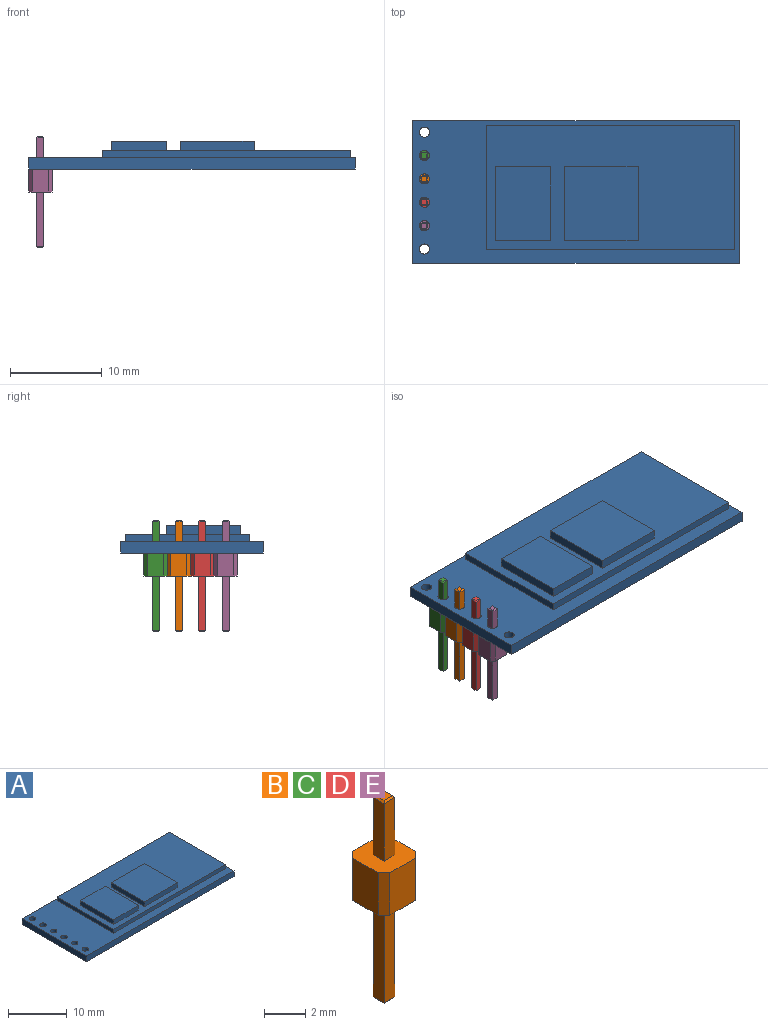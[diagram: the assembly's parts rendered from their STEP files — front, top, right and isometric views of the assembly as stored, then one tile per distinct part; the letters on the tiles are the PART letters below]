
ASSEMBLY  parts=5 mates=1
PART A: 27 faces, bbox 35.5x15.5x3 mm
  f0: plane 27x13.5mm, normal (0,0,1), area 252.5mm2, adj f13,f14,f15,f16,f17,f18,f19,f20
  f1: plane 35.5x1.2mm, normal (0,1,0), area 42.6mm2, adj f2,f10,f11,f12
  f2: plane 15.54x1.2mm, normal (-1,0,0), area 18.6mm2, adj f1,f3,f11,f12
  f3: plane 35.5x1.2mm, normal (0,-1,0), area 42.6mm2, adj f2,f10,f11,f12
  f4: cylinder r=0.55mm len=1.2mm, axis (0,0,-1), area 4.1mm2, adj f11,f12
  f5: cylinder r=0.55mm len=1.2mm, axis (0,0,-1), area 4.1mm2, adj f11,f12
  f6: cylinder r=0.55mm len=1.2mm, axis (0,0,-1), area 4.1mm2, adj f11,f12
  f7: cylinder r=0.55mm len=1.2mm, axis (0,0,-1), area 4.1mm2, adj f11,f12
  f8: cylinder r=0.55mm len=1.2mm, axis (0,0,-1), area 4.1mm2, adj f11,f12
  f9: cylinder r=0.55mm len=1.2mm, axis (0,0,-1), area 4.1mm2, adj f11,f12
  f10: plane 15.54x1.2mm, normal (1,0,0), area 18.6mm2, adj f1,f3,f11,f12
  f11: plane 35.5x15.54mm, normal (0,0,1), area 181.5mm2, adj f1,f2,f3,f4,f5,f6,f7,f8
  f12: plane 35.5x15.54mm, normal (0,0,-1), area 546mm2, adj f1,f2,f3,f4,f5,f6,f7,f8
  f13: plane 13.5x0.8mm, normal (-1,0,0), area 10.8mm2, adj f0,f11,f14,f16
  f14: plane 27x0.8mm, normal (0,-1,0), area 21.6mm2, adj f0,f11,f13,f15
  f15: plane 13.5x0.8mm, normal (1,0,0), area 10.8mm2, adj f0,f11,f14,f16
  f16: plane 27x0.8mm, normal (0,1,0), area 21.6mm2, adj f0,f11,f13,f15
  f17: plane 8x1mm, normal (-1,0,0), area 8mm2, adj f0,f18,f20,f21
  f18: plane 6x1mm, normal (0,-1,0), area 6mm2, adj f0,f17,f19,f21
  f19: plane 8x1mm, normal (1,0,0), area 8mm2, adj f0,f18,f20,f21
  f20: plane 6x1mm, normal (0,1,0), area 6mm2, adj f0,f17,f19,f21
  f21: plane 8x6mm, normal (0,0,1), area 48mm2, adj f17,f18,f19,f20
  f22: plane 8x1mm, normal (-1,0,0), area 8mm2, adj f0,f23,f25,f26
  f23: plane 8x1mm, normal (0,-1,0), area 8mm2, adj f0,f22,f24,f26
  f24: plane 8x1mm, normal (1,0,0), area 8mm2, adj f0,f23,f25,f26
  f25: plane 8x1mm, normal (0,1,0), area 8mm2, adj f0,f22,f24,f26
  f26: plane 8x8mm, normal (0,0,1), area 64mm2, adj f22,f23,f24,f25
PART B: 28 faces, bbox 2.5x2.5x12 mm
  f0: plane 3.4x0.75mm, normal (0,-1,0), area 2.6mm2, adj f1,f3,f5,f13
  f1: plane 3.4x0.75mm, normal (1,0,0), area 2.6mm2, adj f0,f2,f6,f13
  f2: plane 3.4x0.75mm, normal (0,1,0), area 2.6mm2, adj f1,f3,f8,f13
  f3: plane 3.4x0.75mm, normal (-1,0,0), area 2.6mm2, adj f0,f2,f7,f13
  f4: plane 0.55x0.55mm, normal (0,0,1), area 0.3mm2, adj f5,f6,f7,f8
  f5: plane 0.75x0.1mm, normal (0,-0.71,0.71), area 0.1mm2, adj f0,f4,f6,f7
  f6: plane 0.75x0.1mm, normal (0.71,0,0.71), area 0.1mm2, adj f1,f4,f5,f8
  f7: plane 0.75x0.1mm, normal (-0.71,0,0.71), area 0.1mm2, adj f3,f4,f5,f8
  f8: plane 0.75x0.1mm, normal (0,0.71,0.71), area 0.1mm2, adj f2,f4,f6,f7
  f9: plane 2.5x1.74mm, normal (0,-1,0), area 4.4mm2, adj f13,f14,f25,f27
  f10: plane 2.5x1.74mm, normal (1,0,0), area 4.4mm2, adj f13,f14,f24,f25
  f11: plane 2.5x1.74mm, normal (0,1,0), area 4.4mm2, adj f13,f14,f24,f26
  f12: plane 2.5x1.74mm, normal (-1,0,0), area 4.4mm2, adj f13,f14,f26,f27
  f13: plane 2.54x2.54mm, normal (0,0,1), area 5.6mm2, adj f0,f1,f2,f3,f9,f10,f11,f12
  f14: plane 2.54x2.54mm, normal (0,0,-1), area 5.6mm2, adj f9,f10,f11,f12,f20,f21,f22,f23
  f15: plane 0.55x0.55mm, normal (0,0,-1), area 0.3mm2, adj f16,f17,f18,f19
  f16: plane 0.75x0.1mm, normal (0,-0.71,-0.71), area 0.1mm2, adj f15,f17,f19,f23
  f17: plane 0.75x0.1mm, normal (0.71,0,-0.71), area 0.1mm2, adj f15,f16,f18,f22
  f18: plane 0.75x0.1mm, normal (0,0.71,-0.71), area 0.1mm2, adj f15,f17,f19,f21
  f19: plane 0.75x0.1mm, normal (-0.71,0,-0.71), area 0.1mm2, adj f15,f16,f18,f20
  f20: plane 5.9x0.75mm, normal (-1,0,0), area 4.4mm2, adj f14,f19,f21,f23
  f21: plane 5.9x0.75mm, normal (0,1,0), area 4.4mm2, adj f14,f18,f20,f22
  f22: plane 5.9x0.75mm, normal (1,0,0), area 4.4mm2, adj f14,f17,f21,f23
  f23: plane 5.9x0.75mm, normal (0,-1,0), area 4.4mm2, adj f14,f16,f20,f22
  f24: plane 2.5x0.4mm, normal (0.71,0.71,0), area 1.4mm2, adj f10,f11,f13,f14
  f25: plane 2.5x0.4mm, normal (0.71,-0.71,0), area 1.4mm2, adj f9,f10,f13,f14
  f26: plane 2.5x0.4mm, normal (-0.71,0.71,0), area 1.4mm2, adj f11,f12,f13,f14
  f27: plane 2.5x0.4mm, normal (-0.71,-0.71,0), area 1.4mm2, adj f9,f12,f13,f14
PART C: same geometry as B
PART D: same geometry as B
PART E: same geometry as B
PLACE A at identity
PLACE B t=(1.27,9.19,-8.5)mm
PLACE C t=(1.27,11.73,-8.5)mm
PLACE D t=(1.27,6.65,-8.5)mm
PLACE E t=(1.27,4.11,-8.5)mm
MATE fastened C.f13 <-> A.f5  axis (0,0,1) through (1.27,11.73,0)mm
